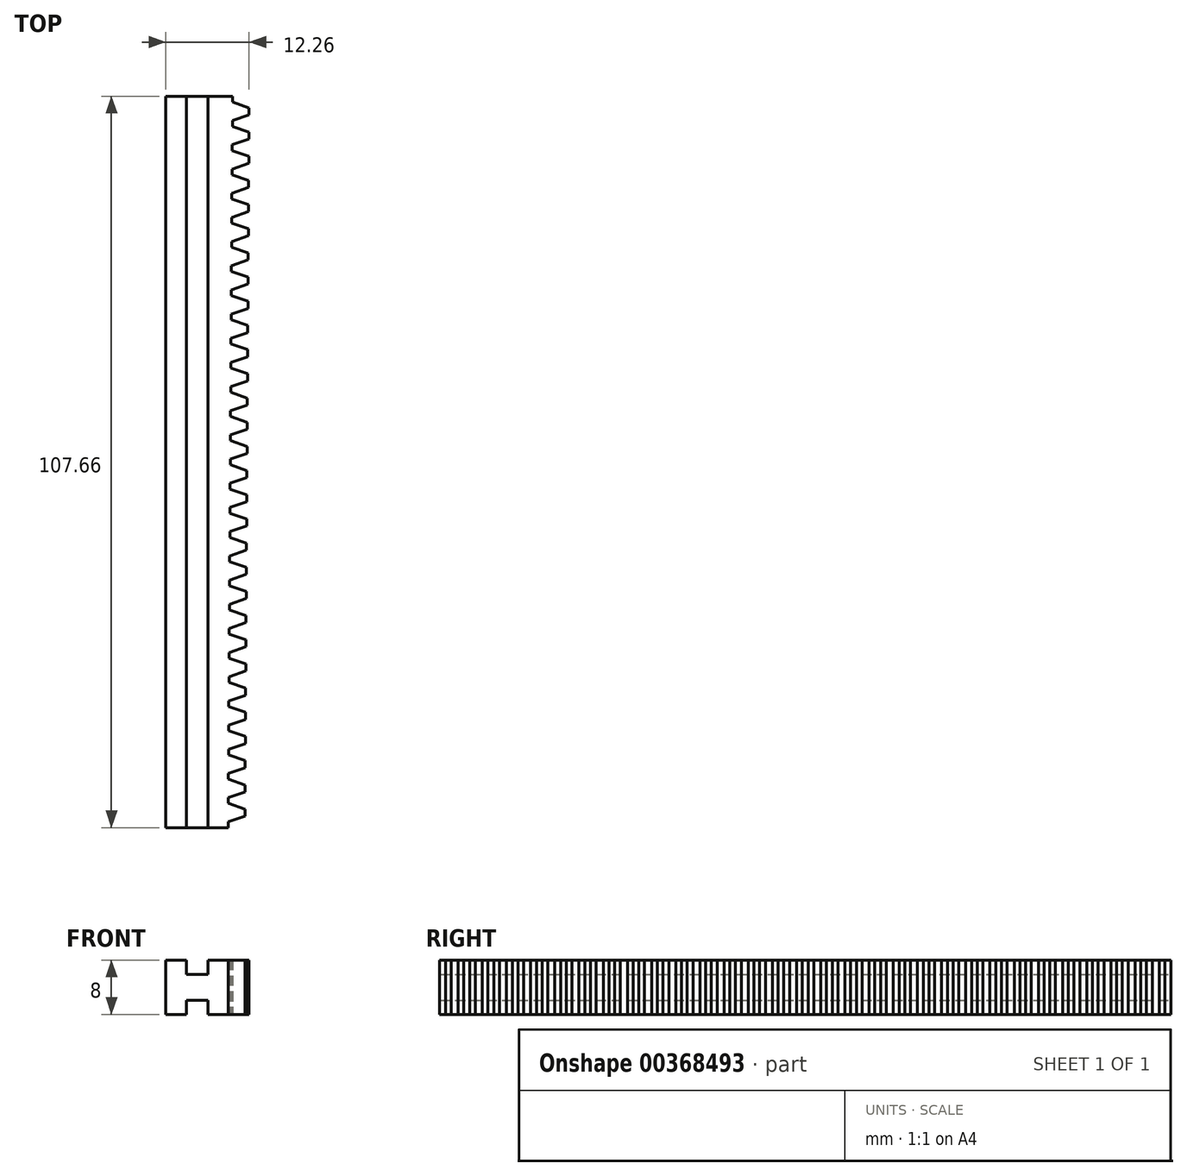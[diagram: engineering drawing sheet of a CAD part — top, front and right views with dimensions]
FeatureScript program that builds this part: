
annotation { "Feature Type Name" : "Feature", "Feature Type Description" : "" }
export const myFeature = defineFeature(function(context is Context, id is Id, definition is map)
    precondition{}
    {
        {
            var Q0;
            Q0=qCreatedBy(makeId("Top.planeOp"),FACE);
            var sketch = newSketch(context, id + "F0", { "sketchPlane" : qUnion([Q0])});
            skPoint(sketch, "E0.bottom.start.orphan", {"position": v(23.3, -0.82) * mm});
            skPoint(sketch, "E1.bottom.start.orphan", {"position": v(23.3, 29.18) * mm});
            skLineSegment(sketch, "E2", {"start": v(-7.66, 12.67) * mm, "end": v(-7.66, 11.82) * mm});
            skLineSegment(sketch, "E3", {"start": v(-7.66, 11.82) * mm, "end": v(-5.2, 10.97) * mm});
            skLineSegment(sketch, "E4", {"start": v(-5.18, 10.46) * mm, "end": v(-8.83, 10.46) * mm, "construction": true});
            skLineSegment(sketch, "E5.MirrorCS", {"start": v(-7.66, 9.1) * mm, "end": v(-5.2, 9.95) * mm});
            skLineSegment(sketch, "E6.MirrorCS", {"start": v(-7.66, 8.25) * mm, "end": v(-7.66, 9.1) * mm});
            skLineSegment(sketch, "E7", {"start": v(-7.66, 8.25) * mm, "end": v(-5.24, 8.25) * mm, "construction": true});
            skLineSegment(sketch, "E8", {"start": v(-5.2, 10.97) * mm, "end": v(-5.2, 9.95) * mm});
            skLineSegment(sketch, "E9.1.0.0", {"start": v(-7.68, 8.26) * mm, "end": v(-5.21, 7.41) * mm});
            skLineSegment(sketch, "E9.1.0.1", {"start": v(-7.68, 4.69) * mm, "end": v(-7.68, 5.54) * mm});
            skLineSegment(sketch, "E9.1.0.2", {"start": v(-7.68, 5.54) * mm, "end": v(-5.21, 6.39) * mm});
            skLineSegment(sketch, "E9.1.0.3", {"start": v(-5.21, 7.41) * mm, "end": v(-5.21, 6.39) * mm});
            skLineSegment(sketch, "E9.2.0.0", {"start": v(-7.7, 4.7) * mm, "end": v(-5.24, 3.85) * mm});
            skLineSegment(sketch, "E9.2.0.1", {"start": v(-7.7, 1.13) * mm, "end": v(-7.7, 1.98) * mm});
            skLineSegment(sketch, "E9.2.0.2", {"start": v(-7.7, 1.98) * mm, "end": v(-5.24, 2.83) * mm});
            skLineSegment(sketch, "E9.2.0.3", {"start": v(-5.24, 3.85) * mm, "end": v(-5.24, 2.83) * mm});
            skLineSegment(sketch, "E9.3.0.0", {"start": v(-7.72, 1.14) * mm, "end": v(-5.26, 0.3) * mm});
            skLineSegment(sketch, "E9.3.0.1", {"start": v(-7.72, -2.43) * mm, "end": v(-7.72, -1.58) * mm});
            skLineSegment(sketch, "E9.3.0.2", {"start": v(-7.72, -1.58) * mm, "end": v(-5.26, -0.73) * mm});
            skLineSegment(sketch, "E9.3.0.3", {"start": v(-5.26, 0.3) * mm, "end": v(-5.26, -0.73) * mm});
            skLineSegment(sketch, "E9.4.0.0", {"start": v(-7.74, -2.42) * mm, "end": v(-5.28, -3.27) * mm});
            skLineSegment(sketch, "E9.4.0.1", {"start": v(-7.74, -6) * mm, "end": v(-7.74, -5.14) * mm});
            skLineSegment(sketch, "E9.4.0.2", {"start": v(-7.74, -5.14) * mm, "end": v(-5.28, -4.3) * mm});
            skLineSegment(sketch, "E9.4.0.3", {"start": v(-5.28, -3.27) * mm, "end": v(-5.28, -4.3) * mm});
            skLineSegment(sketch, "E9.5.0.0", {"start": v(-7.76, -5.98) * mm, "end": v(-5.3, -6.83) * mm});
            skLineSegment(sketch, "E9.5.0.1", {"start": v(-7.76, -9.55) * mm, "end": v(-7.76, -8.7) * mm});
            skLineSegment(sketch, "E9.5.0.2", {"start": v(-7.76, -8.7) * mm, "end": v(-5.3, -7.85) * mm});
            skLineSegment(sketch, "E9.5.0.3", {"start": v(-5.3, -6.83) * mm, "end": v(-5.3, -7.85) * mm});
            skLineSegment(sketch, "E9.6.0.0", {"start": v(-7.79, -9.54) * mm, "end": v(-5.32, -10.39) * mm});
            skLineSegment(sketch, "E9.6.0.1", {"start": v(-7.79, -13.11) * mm, "end": v(-7.79, -12.26) * mm});
            skLineSegment(sketch, "E9.6.0.2", {"start": v(-7.79, -12.26) * mm, "end": v(-5.32, -11.41) * mm});
            skLineSegment(sketch, "E9.6.0.3", {"start": v(-5.32, -10.39) * mm, "end": v(-5.32, -11.41) * mm});
            skLineSegment(sketch, "E9.7.0.0", {"start": v(-7.8, -13.1) * mm, "end": v(-5.34, -13.95) * mm});
            skLineSegment(sketch, "E9.7.0.1", {"start": v(-7.8, -16.67) * mm, "end": v(-7.8, -15.82) * mm});
            skLineSegment(sketch, "E9.7.0.2", {"start": v(-7.8, -15.82) * mm, "end": v(-5.34, -14.97) * mm});
            skLineSegment(sketch, "E9.7.0.3", {"start": v(-5.34, -13.95) * mm, "end": v(-5.34, -14.97) * mm});
            skLineSegment(sketch, "E9.8.0.0", {"start": v(-7.83, -16.66) * mm, "end": v(-5.36, -17.5) * mm});
            skLineSegment(sketch, "E9.8.0.1", {"start": v(-7.83, -20.23) * mm, "end": v(-7.83, -19.38) * mm});
            skLineSegment(sketch, "E9.8.0.2", {"start": v(-7.83, -19.38) * mm, "end": v(-5.36, -18.53) * mm});
            skLineSegment(sketch, "E9.8.0.3", {"start": v(-5.36, -17.5) * mm, "end": v(-5.36, -18.53) * mm});
            skLineSegment(sketch, "E9.9.0.0", {"start": v(-7.85, -20.22) * mm, "end": v(-5.39, -21.07) * mm});
            skLineSegment(sketch, "E9.9.0.1", {"start": v(-7.85, -23.8) * mm, "end": v(-7.85, -22.94) * mm});
            skLineSegment(sketch, "E9.9.0.2", {"start": v(-7.85, -22.94) * mm, "end": v(-5.39, -22.1) * mm});
            skLineSegment(sketch, "E9.9.0.3", {"start": v(-5.39, -21.07) * mm, "end": v(-5.39, -22.1) * mm});
            skLineSegment(sketch, "E9.direction1", {"start": v(-7.66, 11.82) * mm, "end": v(-7.68, 8.26) * mm, "construction": true});
            skLineSegment(sketch, "E10", {"start": v(-7.66, 12.67) * mm, "end": v(-11.25, 12.67) * mm});
            skLineSegment(sketch, "E11.0.10.0", {"start": v(-7.87, -23.78) * mm, "end": v(-5.4, -24.63) * mm});
            skLineSegment(sketch, "E11.3.10.0", {"start": v(-7.87, -27.35) * mm, "end": v(-7.87, -26.5) * mm});
            skLineSegment(sketch, "E11.6.10.0", {"start": v(-7.87, -26.5) * mm, "end": v(-5.4, -25.65) * mm});
            skLineSegment(sketch, "E11.9.10.0", {"start": v(-5.4, -24.63) * mm, "end": v(-5.4, -25.65) * mm});
            skLineSegment(sketch, "E11.0.11.0", {"start": v(-7.9, -27.34) * mm, "end": v(-5.43, -28.19) * mm});
            skLineSegment(sketch, "E11.3.11.0", {"start": v(-7.9, -30.91) * mm, "end": v(-7.9, -30.06) * mm});
            skLineSegment(sketch, "E11.6.11.0", {"start": v(-7.9, -30.06) * mm, "end": v(-5.43, -29.21) * mm});
            skLineSegment(sketch, "E11.9.11.0", {"start": v(-5.43, -28.19) * mm, "end": v(-5.43, -29.21) * mm});
            skLineSegment(sketch, "E11.0.12.0", {"start": v(-7.91, -30.9) * mm, "end": v(-5.45, -31.75) * mm});
            skLineSegment(sketch, "E11.3.12.0", {"start": v(-7.91, -34.47) * mm, "end": v(-7.91, -33.62) * mm});
            skLineSegment(sketch, "E11.6.12.0", {"start": v(-7.91, -33.62) * mm, "end": v(-5.45, -32.77) * mm});
            skLineSegment(sketch, "E11.9.12.0", {"start": v(-5.45, -31.75) * mm, "end": v(-5.45, -32.77) * mm});
            skLineSegment(sketch, "E11.0.13.0", {"start": v(-7.93, -34.46) * mm, "end": v(-5.47, -35.3) * mm});
            skLineSegment(sketch, "E11.3.13.0", {"start": v(-7.93, -38.03) * mm, "end": v(-7.93, -37.18) * mm});
            skLineSegment(sketch, "E11.6.13.0", {"start": v(-7.93, -37.18) * mm, "end": v(-5.47, -36.33) * mm});
            skLineSegment(sketch, "E11.9.13.0", {"start": v(-5.47, -35.3) * mm, "end": v(-5.47, -36.33) * mm});
            skLineSegment(sketch, "E11.0.14.0", {"start": v(-7.96, -38.02) * mm, "end": v(-5.5, -38.86) * mm});
            skLineSegment(sketch, "E11.3.14.0", {"start": v(-7.96, -41.59) * mm, "end": v(-7.96, -40.74) * mm});
            skLineSegment(sketch, "E11.6.14.0", {"start": v(-7.96, -40.74) * mm, "end": v(-5.5, -39.9) * mm});
            skLineSegment(sketch, "E11.9.14.0", {"start": v(-5.5, -38.86) * mm, "end": v(-5.5, -39.9) * mm});
            skLineSegment(sketch, "E11.0.15.0", {"start": v(-7.98, -41.58) * mm, "end": v(-5.51, -42.42) * mm});
            skLineSegment(sketch, "E11.3.15.0", {"start": v(-7.98, -45.15) * mm, "end": v(-7.98, -44.3) * mm});
            skLineSegment(sketch, "E11.6.15.0", {"start": v(-7.98, -44.3) * mm, "end": v(-5.51, -43.45) * mm});
            skLineSegment(sketch, "E11.9.15.0", {"start": v(-5.51, -42.42) * mm, "end": v(-5.51, -43.45) * mm});
            skLineSegment(sketch, "E11.0.16.0", {"start": v(-8, -45.14) * mm, "end": v(-5.54, -45.98) * mm});
            skLineSegment(sketch, "E11.3.16.0", {"start": v(-8, -48.7) * mm, "end": v(-8, -47.86) * mm});
            skLineSegment(sketch, "E11.6.16.0", {"start": v(-8, -47.86) * mm, "end": v(-5.54, -47.01) * mm});
            skLineSegment(sketch, "E11.9.16.0", {"start": v(-5.54, -45.98) * mm, "end": v(-5.54, -47.01) * mm});
            skLineSegment(sketch, "E11.0.17.0", {"start": v(-8.02, -48.7) * mm, "end": v(-5.56, -49.54) * mm});
            skLineSegment(sketch, "E11.3.17.0", {"start": v(-8.02, -52.27) * mm, "end": v(-8.02, -51.42) * mm});
            skLineSegment(sketch, "E11.6.17.0", {"start": v(-8.02, -51.42) * mm, "end": v(-5.56, -50.57) * mm});
            skLineSegment(sketch, "E11.9.17.0", {"start": v(-5.56, -49.54) * mm, "end": v(-5.56, -50.57) * mm});
            skLineSegment(sketch, "E11.0.18.0", {"start": v(-8.04, -52.26) * mm, "end": v(-5.58, -53.1) * mm});
            skLineSegment(sketch, "E11.3.18.0", {"start": v(-8.04, -55.83) * mm, "end": v(-8.04, -54.98) * mm});
            skLineSegment(sketch, "E11.6.18.0", {"start": v(-8.04, -54.98) * mm, "end": v(-5.58, -54.13) * mm});
            skLineSegment(sketch, "E11.9.18.0", {"start": v(-5.58, -53.1) * mm, "end": v(-5.58, -54.13) * mm});
            skLineSegment(sketch, "E11.0.19.0", {"start": v(-8.06, -55.82) * mm, "end": v(-5.6, -56.66) * mm});
            skLineSegment(sketch, "E11.3.19.0", {"start": v(-8.06, -59.39) * mm, "end": v(-8.06, -58.54) * mm});
            skLineSegment(sketch, "E11.6.19.0", {"start": v(-8.06, -58.54) * mm, "end": v(-5.6, -57.7) * mm});
            skLineSegment(sketch, "E11.9.19.0", {"start": v(-5.6, -56.66) * mm, "end": v(-5.6, -57.7) * mm});
            skLineSegment(sketch, "E11.0.20.0", {"start": v(-8.08, -59.38) * mm, "end": v(-5.62, -60.22) * mm});
            skLineSegment(sketch, "E11.3.20.0", {"start": v(-8.08, -62.95) * mm, "end": v(-8.08, -62.1) * mm});
            skLineSegment(sketch, "E11.6.20.0", {"start": v(-8.08, -62.1) * mm, "end": v(-5.62, -61.25) * mm});
            skLineSegment(sketch, "E11.9.20.0", {"start": v(-5.62, -60.22) * mm, "end": v(-5.62, -61.25) * mm});
            skLineSegment(sketch, "E11.0.21.0", {"start": v(-8.1, -62.94) * mm, "end": v(-5.64, -63.78) * mm});
            skLineSegment(sketch, "E11.3.21.0", {"start": v(-8.1, -66.5) * mm, "end": v(-8.1, -65.66) * mm});
            skLineSegment(sketch, "E11.6.21.0", {"start": v(-8.1, -65.66) * mm, "end": v(-5.64, -64.81) * mm});
            skLineSegment(sketch, "E11.9.21.0", {"start": v(-5.64, -63.78) * mm, "end": v(-5.64, -64.81) * mm});
            skLineSegment(sketch, "E11.0.22.0", {"start": v(-8.13, -66.5) * mm, "end": v(-5.66, -67.34) * mm});
            skLineSegment(sketch, "E11.3.22.0", {"start": v(-8.13, -70.07) * mm, "end": v(-8.13, -69.22) * mm});
            skLineSegment(sketch, "E11.6.22.0", {"start": v(-8.13, -69.22) * mm, "end": v(-5.66, -68.37) * mm});
            skLineSegment(sketch, "E11.9.22.0", {"start": v(-5.66, -67.34) * mm, "end": v(-5.66, -68.37) * mm});
            skLineSegment(sketch, "E11.0.23.0", {"start": v(-8.15, -70.05) * mm, "end": v(-5.68, -70.9) * mm});
            skLineSegment(sketch, "E11.3.23.0", {"start": v(-8.15, -73.63) * mm, "end": v(-8.15, -72.78) * mm});
            skLineSegment(sketch, "E11.6.23.0", {"start": v(-8.15, -72.78) * mm, "end": v(-5.68, -71.93) * mm});
            skLineSegment(sketch, "E11.9.23.0", {"start": v(-5.68, -70.9) * mm, "end": v(-5.68, -71.93) * mm});
            skLineSegment(sketch, "E11.0.24.0", {"start": v(-8.17, -73.61) * mm, "end": v(-5.7, -74.46) * mm});
            skLineSegment(sketch, "E11.3.24.0", {"start": v(-8.17, -77.19) * mm, "end": v(-8.17, -76.34) * mm});
            skLineSegment(sketch, "E11.6.24.0", {"start": v(-8.17, -76.34) * mm, "end": v(-5.7, -75.5) * mm});
            skLineSegment(sketch, "E11.9.24.0", {"start": v(-5.7, -74.46) * mm, "end": v(-5.7, -75.5) * mm});
            skLineSegment(sketch, "E11.0.25.0", {"start": v(-8.2, -77.17) * mm, "end": v(-5.73, -78.02) * mm});
            skLineSegment(sketch, "E11.3.25.0", {"start": v(-8.2, -80.75) * mm, "end": v(-8.2, -79.9) * mm});
            skLineSegment(sketch, "E11.6.25.0", {"start": v(-8.2, -79.9) * mm, "end": v(-5.73, -79.05) * mm});
            skLineSegment(sketch, "E11.9.25.0", {"start": v(-5.73, -78.02) * mm, "end": v(-5.73, -79.05) * mm});
            skLineSegment(sketch, "E11.0.26.0", {"start": v(-8.21, -80.73) * mm, "end": v(-5.75, -81.58) * mm});
            skLineSegment(sketch, "E11.3.26.0", {"start": v(-8.21, -84.3) * mm, "end": v(-8.21, -83.46) * mm});
            skLineSegment(sketch, "E11.6.26.0", {"start": v(-8.21, -83.46) * mm, "end": v(-5.75, -82.61) * mm});
            skLineSegment(sketch, "E11.9.26.0", {"start": v(-5.75, -81.58) * mm, "end": v(-5.75, -82.61) * mm});
            skLineSegment(sketch, "E11.0.27.0", {"start": v(-8.23, -84.3) * mm, "end": v(-5.77, -85.14) * mm});
            skLineSegment(sketch, "E11.3.27.0", {"start": v(-8.23, -87.87) * mm, "end": v(-8.23, -87.02) * mm});
            skLineSegment(sketch, "E11.6.27.0", {"start": v(-8.23, -87.02) * mm, "end": v(-5.77, -86.17) * mm});
            skLineSegment(sketch, "E11.9.27.0", {"start": v(-5.77, -85.14) * mm, "end": v(-5.77, -86.17) * mm});
            skLineSegment(sketch, "E11.0.28.0", {"start": v(-8.26, -87.85) * mm, "end": v(-5.8, -88.7) * mm});
            skLineSegment(sketch, "E11.3.28.0", {"start": v(-8.26, -91.43) * mm, "end": v(-8.26, -90.58) * mm});
            skLineSegment(sketch, "E11.6.28.0", {"start": v(-8.26, -90.58) * mm, "end": v(-5.8, -89.73) * mm});
            skLineSegment(sketch, "E11.9.28.0", {"start": v(-5.8, -88.7) * mm, "end": v(-5.8, -89.73) * mm});
            skLineSegment(sketch, "E11.0.29.0", {"start": v(-8.28, -91.41) * mm, "end": v(-5.81, -92.26) * mm});
            skLineSegment(sketch, "E11.3.29.0", {"start": v(-8.28, -94.99) * mm, "end": v(-8.28, -94.14) * mm});
            skLineSegment(sketch, "E11.6.29.0", {"start": v(-8.28, -94.14) * mm, "end": v(-5.81, -93.3) * mm});
            skLineSegment(sketch, "E11.9.29.0", {"start": v(-5.81, -92.26) * mm, "end": v(-5.81, -93.3) * mm});
            skLineSegment(sketch, "E12", {"start": v(-11.25, 12.67) * mm, "end": v(-11.25, -94.99) * mm});
            skLineSegment(sketch, "E13", {"start": v(-11.25, -94.99) * mm, "end": v(-8.28, -94.99) * mm});
            skPoint(sketch, "E14.start.orphan", {"position": v(-9.4, -23.8) * mm});
            skSolve(sketch);
        }
        {
            var Q0;
            Q0=makeQuery(id+"F0.imprint","IMPRINT",FACE,{"disambiguationData":[TD([[makeQuery(id+"F0.imprint","IMPRINT",EDGE,{"derivedFrom":sQuery(id+"F0.wireOp",EDGE,"E2")}),-1.0]])]});
            extrude(context, id + "F1", {"entities" : qUnion([Q0]), "depth" : 8 * mm});
        }
        {
            var Q0;
            Q0=makeQuery(id+"F1.opExtrude","SWEPT_FACE",FACE,{"disambiguationData":[OSD([sQuery(id+"F0.wireOp",EDGE,"E12")])]});
            var sketch = newSketch(context, id + "F2", { "sketchPlane" : qUnion([Q0])});
            skLineSegment(sketch, "E15.bottom", {"start": v(94.99, 5.9) * mm, "end": v(-12.67, 5.9) * mm});
            skLineSegment(sketch, "E15.top", {"start": v(94.99, 2.1) * mm, "end": v(-12.67, 2.1) * mm});
            skLineSegment(sketch, "E15.left", {"start": v(94.99, 5.9) * mm, "end": v(94.99, 2.1) * mm});
            skLineSegment(sketch, "E15.right", {"start": v(-12.67, 5.9) * mm, "end": v(-12.67, 2.1) * mm});
            skPoint(sketch, "E15.middle", {"position": v(41.16, 4) * mm});
            skPoint(sketch, "E15.middle.positionSnap0", {"position": v(94.99, 4) * mm});
            skPoint(sketch, "E15.middle.positionSnap1", {"position": v(41.16, 0) * mm});
            skPoint(sketch, "E15.centerSnap0", {"position": v(94.99, 4) * mm});
            skPoint(sketch, "E15.centerSnap1", {"position": v(41.16, 0) * mm});
            skSolve(sketch);
        }
        {
            var Q0;
            Q0=makeQuery(id+"F2.imprint","IMPRINT",FACE,{"disambiguationData":[TD([[makeQuery(id+"F2.imprint","IMPRINT",EDGE,{"derivedFrom":sQuery(id+"F2.wireOp",EDGE,"E15.bottom")}),1.0]])]});
            extrude(context, id + "F3", {"entities" : qUnion([Q0]), "operationType" : NewBodyOperationType.ADD, "depth" : 3.2 * mm});
        }
        {
            var Q0;
            Q0=makeQuery(id+"F3.opExtrude","CAP_FACE",FACE,{"disambiguationData":[OSD([sQuery(id+"F2.wireOp",EDGE,"E15.bottom"),sQuery(id+"F2.wireOp",EDGE,"E15.top"),sQuery(id+"F2.wireOp",EDGE,"E15.left"),sQuery(id+"F2.wireOp",EDGE,"E15.right")])],"isStart":false});
            var sketch = newSketch(context, id + "F4", { "sketchPlane" : qUnion([Q0])});
            skLineSegment(sketch, "E16.bottom", {"start": v(-12.67, 8) * mm, "end": v(94.99, 8) * mm});
            skLineSegment(sketch, "E16.top", {"start": v(-12.67, 0) * mm, "end": v(94.99, 0) * mm});
            skLineSegment(sketch, "E16.left", {"start": v(-12.67, 8) * mm, "end": v(-12.67, 0) * mm});
            skLineSegment(sketch, "E16.right", {"start": v(94.99, 8) * mm, "end": v(94.99, 0) * mm});
            skPoint(sketch, "E16.middle", {"position": v(41.16, 4) * mm});
            skPoint(sketch, "E16.middle.positionSnap0", {"position": v(41.16, 2.1) * mm});
            skPoint(sketch, "E16.middle.positionSnap1", {"position": v(94.99, 4) * mm});
            skPoint(sketch, "E16.centerSnap0", {"position": v(41.16, 2.1) * mm});
            skPoint(sketch, "E16.centerSnap1", {"position": v(94.99, 4) * mm});
            skSolve(sketch);
        }
        {
            var Q0;
            {var subQ0=sQuery(id+"F4.wireOp",EDGE,"E16.bottom");Q0=makeQuery(id+"F4.imprint","IMPRINT",FACE,{"disambiguationData":[TD([[makeQuery(id+"F4.imprint","IMPRINT",EDGE,{"derivedFrom":subQ0}),-1.0]])]});}
            var Q1;
            {var subQ1=makeQuery(id+"F3.opExtrude","CAP_EDGE",EDGE,{"disambiguationData":[OSD([sQuery(id+"F2.wireOp",EDGE,"E15.bottom")])],"isStart":false});Q1=makeQuery(id+"F4.imprint","IMPRINT",FACE,{"disambiguationData":[TD([[makeQuery(id+"F4.imprint","IMPRINT",EDGE,{"derivedFrom":subQ1}),1.0]])]});}
            var Q2;
            {var subQ0=sQuery(id+"F4.wireOp",EDGE,"E16.top");Q2=makeQuery(id+"F4.imprint","IMPRINT",FACE,{"disambiguationData":[TD([[makeQuery(id+"F4.imprint","IMPRINT",EDGE,{"derivedFrom":subQ0}),1.0]])]});}
            extrude(context, id + "F5", {"entities" : qUnion([Q0, Q1, Q2]), "operationType" : NewBodyOperationType.ADD, "depth" : 3 * mm});
        }
    });
